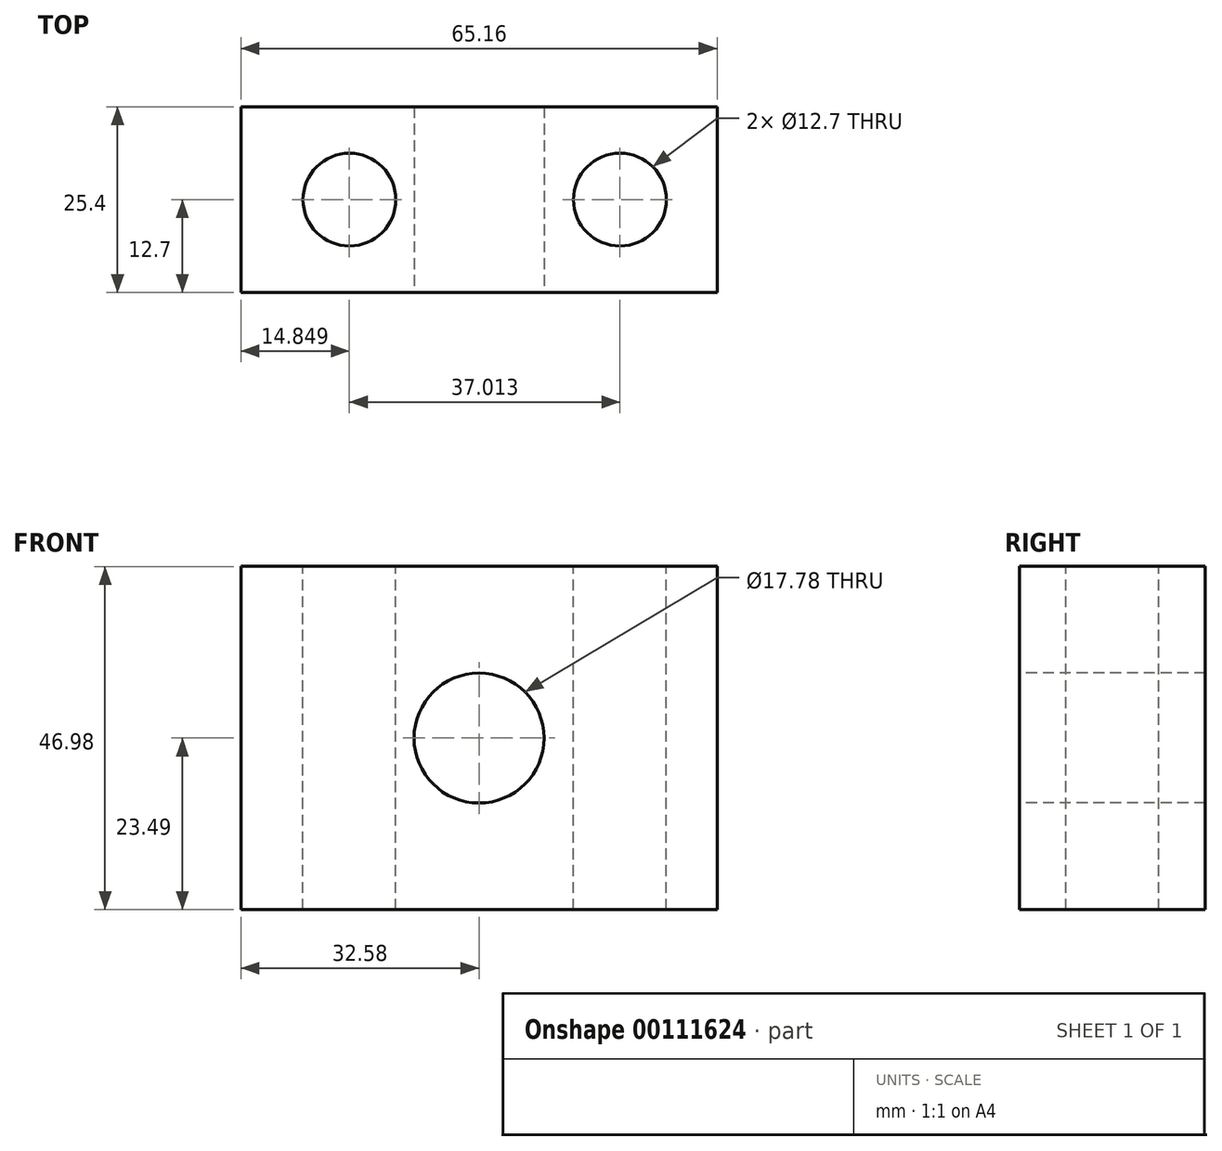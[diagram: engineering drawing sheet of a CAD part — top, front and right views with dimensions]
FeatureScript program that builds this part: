
annotation { "Feature Type Name" : "Feature", "Feature Type Description" : "" }
export const myFeature = defineFeature(function(context is Context, id is Id, definition is map)
    precondition{}
    {
        {
            var Q0;
            Q0=qCreatedBy(makeId("Front.planeOp"),FACE);
            var sketch = newSketch(context, id + "F0", { "sketchPlane" : qUnion([Q0])});
            skLineSegment(sketch, "E0.bottom", {"start": v(32.58, -23.5) * mm, "end": v(-32.58, -23.5) * mm});
            skLineSegment(sketch, "E0.top", {"start": v(32.58, 23.5) * mm, "end": v(-32.58, 23.5) * mm});
            skLineSegment(sketch, "E0.left", {"start": v(32.58, -23.5) * mm, "end": v(32.58, 23.5) * mm});
            skLineSegment(sketch, "E0.right", {"start": v(-32.58, -23.5) * mm, "end": v(-32.58, 23.5) * mm});
            skPoint(sketch, "E0.middle", {"position": v(0, 0) * mm});
            skSolve(sketch);
        }
        {
            var Q0;
            Q0=makeQuery(id+"F0.imprint","IMPRINT",FACE,{"disambiguationData":[TD([[makeQuery(id+"F0.imprint","IMPRINT",EDGE,{"derivedFrom":sQuery(id+"F0.wireOp",EDGE,"E0.bottom")}),-1.0]])]});
            extrude(context, id + "F1", {"entities" : qUnion([Q0]), "depth" : 25.4 * mm});
        }
        {
            var Q0;
            Q0=makeQuery(id+"F1.opExtrude","CAP_FACE",FACE,{"disambiguationData":[OSD([sQuery(id+"F0.wireOp",EDGE,"E0.bottom"),sQuery(id+"F0.wireOp",EDGE,"E0.top"),sQuery(id+"F0.wireOp",EDGE,"E0.left"),sQuery(id+"F0.wireOp",EDGE,"E0.right")])],"isStart":false});
            var sketch = newSketch(context, id + "F2", { "sketchPlane" : qUnion([Q0])});
            skCircle(sketch, "E1", {"center": v(0, 0) * mm, "radius": 7.68 * mm});
            skSolve(sketch);
        }
        {
            var Q0;
            Q0=sQuery(id+"F2.wireOp",VERTEX,"E1.center");
            var Q1;
            Q1=makeQuery(id+"F1.opExtrude","SWEPT_BODY",BODY,{"disambiguationData":[OSD([sQuery(id+"F0.wireOp",EDGE,"E0.bottom"),sQuery(id+"F0.wireOp",EDGE,"E0.top"),sQuery(id+"F0.wireOp",EDGE,"E0.left"),sQuery(id+"F0.wireOp",EDGE,"E0.right")])]});
            hole(context, id + "F3", {"style" : HoleStyle.SIMPLE, "endStyle" : HoleEndStyle.THROUGH, "holeDiameter" : 17.78 * mm, "locations" : qUnion([Q0]), "scope" : qUnion([Q1]), "isTappedThrough" : true});
        }
        {
            var Q0;
            Q0=makeQuery(id+"F1.opExtrude","SWEPT_FACE",FACE,{"disambiguationData":[OSD([sQuery(id+"F0.wireOp",EDGE,"E0.top")])]});
            var sketch = newSketch(context, id + "F4", { "sketchPlane" : qUnion([Q0])});
            skCircle(sketch, "E2", {"center": v(-17.73, -12.7) * mm, "radius": 5.17 * mm});
            skPoint(sketch, "E2.centerSnap0", {"position": v(-32.58, -12.7) * mm});
            skCircle(sketch, "E3", {"center": v(17.5, -12.7) * mm, "radius": 4.95 * mm});
            skPoint(sketch, "E3.centerSnap0", {"position": v(32.58, -12.7) * mm});
            skSolve(sketch);
        }
        {
            var Q0;
            Q0=sQuery(id+"F4.wireOp",VERTEX,"E2.center");
            var Q1;
            Q1=makeQuery(id+"F1.opExtrude","SWEPT_BODY",BODY,{"disambiguationData":[OSD([sQuery(id+"F0.wireOp",EDGE,"E0.bottom"),sQuery(id+"F0.wireOp",EDGE,"E0.top"),sQuery(id+"F0.wireOp",EDGE,"E0.left"),sQuery(id+"F0.wireOp",EDGE,"E0.right")])]});
            hole(context, id + "F5", {"style" : HoleStyle.SIMPLE, "endStyle" : HoleEndStyle.THROUGH, "holeDiameter" : 12.7 * mm, "locations" : qUnion([Q0]), "scope" : qUnion([Q1]), "isTappedThrough" : true});
        }
        {
            var Q0;
            Q0=makeQuery(id+"F1.opExtrude","SWEPT_FACE",FACE,{"disambiguationData":[OSD([sQuery(id+"F0.wireOp",EDGE,"E0.top")])]});
            var sketch = newSketch(context, id + "F6", { "sketchPlane" : qUnion([Q0])});
            skCircle(sketch, "E4", {"center": v(19.28, -12.7) * mm, "radius": 6.12 * mm});
            skPoint(sketch, "E4.centerSnap0", {"position": v(32.58, -12.7) * mm});
            skSolve(sketch);
        }
        {
            var Q0;
            Q0=sQuery(id+"F6.wireOp",VERTEX,"E4.center");
            var Q1;
            Q1=makeQuery(id+"F1.opExtrude","SWEPT_BODY",BODY,{"disambiguationData":[OSD([sQuery(id+"F0.wireOp",EDGE,"E0.bottom"),sQuery(id+"F0.wireOp",EDGE,"E0.top"),sQuery(id+"F0.wireOp",EDGE,"E0.left"),sQuery(id+"F0.wireOp",EDGE,"E0.right")])]});
            hole(context, id + "F7", {"style" : HoleStyle.SIMPLE, "endStyle" : HoleEndStyle.THROUGH, "holeDiameter" : 12.7 * mm, "locations" : qUnion([Q0]), "scope" : qUnion([Q1]), "isTappedThrough" : true});
        }
    });
